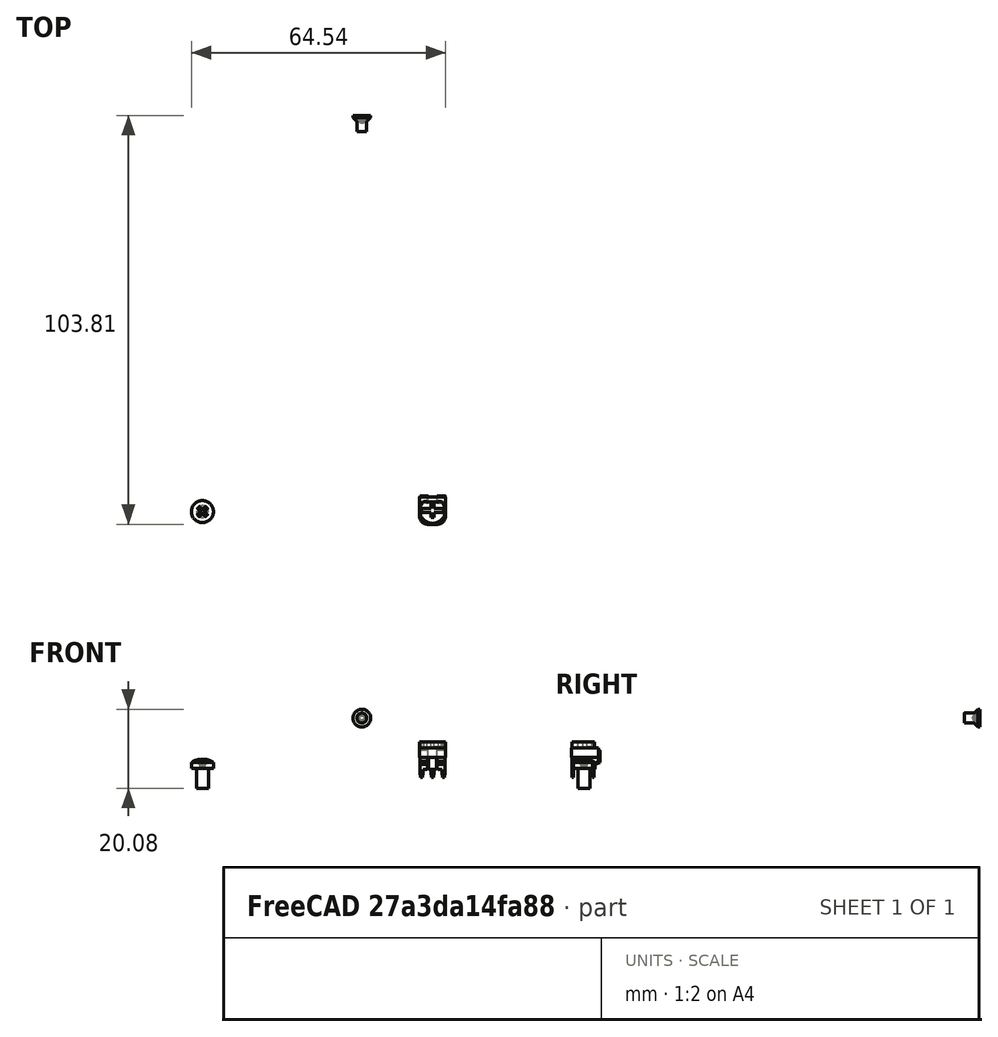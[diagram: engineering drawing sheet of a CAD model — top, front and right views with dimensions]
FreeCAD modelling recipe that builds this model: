
FCSTD DOCUMENT  (FreeCAD 0.19R23058 (Git))
Label: assembly
License: All rights reserved
LicenseURL: http://en.wikipedia.org/wiki/All_rights_reserved
objects: App::Link×8, PartDesign::CoordinateSystem×4, App::Part×4, PartDesign::Point×3, App::VRMLObject×3, App::DocumentObjectGroup×2, Part::FeaturePython×2, App::FeaturePython×1, Part::Feature×1
note: 10 computed .brp shape members not serialized (recipe doc carries the construction recipe); baked Part::Feature solids carry a one-line shape summary decoded from their .brp
EXTERNAL_REF file=parts/bottom_shell.FCStd obj=LCS_1
EXTERNAL_REF file=parts/bottom_shell.FCStd obj=Body
EXTERNAL_REF file=parts/bottom_shell.FCStd obj=HoleAxis_2
EXTERNAL_REF file=parts/top_shell.FCStd obj=HoleAxis_1
EXTERNAL_REF file=parts/top_shell.FCStd obj=Body
EXTERNAL_REF file=parts/board.FCStd obj=HoleAxis_1
EXTERNAL_REF file=parts/bottom_shell.FCStd obj=HoleAxis_16
EXTERNAL_REF file=parts/board.FCStd obj=Body
EXTERNAL_REF file=parts/top_shell.FCStd obj=Label_1
EXTERNAL_REF file=parts/top_shell.FCStd obj=Point_1
EXTERNAL_REF file=parts/bottom_shell.FCStd obj=Label_1
EXTERNAL_REF file=HB9500/assembly.FCStd obj=Contact_1
EXTERNAL_REF file=parts/board.FCStd obj=HoleAxis_2
EXTERNAL_REF file=HB9500/assembly.FCStd obj=Model
EXTERNAL_REF file=parts/top_shell.FCStd obj=HoleAxis_3
EXTERNAL_REF file=parts/top_shell.FCStd obj=HoleAxis_2
EXTERNAL_REF file=parts/bottom_shell.FCStd obj=HoleAxis_1

FEATURE [PartDesign::CoordinateSystem] LCS_Origin
  AttacherType = Attacher::AttachEngine3D
  MapMode = 2
  Support = -> [X_Axis]
FEATURE [App::DocumentObjectGroup] Constraints
FEATURE [App::FeaturePython] Variables  # WARN: FeaturePython — macro-defined, semantics opaque (R4)
FEATURE [App::Link] bottom_shell_Body
  AssemblyType = Asm4EE
  AttachedBy = #LCS_1
  AttachedTo = Parent Assembly#LCS_Origin
  LinkedObject = -> <external parts/bottom_shell.FCStd>#Body
  expr: Placement = LCS_Origin.Placement * AttachmentOffset * bottom_shell#LCS_1.Placement ^ -1
FEATURE [App::Link] top_shell_Body
  AssemblyType = Asm4EE
  AttachedBy = #HoleAxis_1
  AttachedTo = bottom_shell_Body#HoleAxis_2
  LinkPlacement = pos=(0.25,6.58371,36) rot=(0,0,1;0rad)
  LinkedObject = -> <external parts/top_shell.FCStd>#Body
  Placement = pos=(0.25,6.58371,36) rot=(0,0,1;0rad)
  expr: Placement = bottom_shell_Body.Placement * bottom_shell#HoleAxis_2.Placement * AttachmentOffset * top_shell#HoleAxis_1.Placement ^ -1
FEATURE [App::Link] board_Body
  AssemblyType = Asm4EE
  AttachedBy = #HoleAxis_1
  AttachedTo = bottom_shell_Body#HoleAxis_16
  AttachmentOffset = pos=(0,0,0) rot=(0,0,1;3.14159rad)
  LinkPlacement = pos=(0.5,-2,6) rot=(0,0,1;0rad)
  LinkedObject = -> <external parts/board.FCStd>#Body
  Placement = pos=(0.5,-2,6) rot=(0,0,1;0rad)
  expr: Placement = bottom_shell_Body.Placement * bottom_shell#HoleAxis_16.Placement * AttachmentOffset * board#HoleAxis_1.Placement ^ -1
FEATURE [Part::Feature] Part__Feature  label="Potentiometer Blue"
  Placement = pos=(25.4437,-49.9766,10.5) rot=(0,0,1;1.5708rad)
  shape: bbox 6.6 x 7.2 x 9 mm, 74 faces, 2 solids (baked)
FEATURE [PartDesign::Point] Point_1
  AttacherType = Attacher::AttachEnginePoint
  Placement = pos=(-32,-36.6163,25.5) rot=(0,0,1;0rad)
  expr: Placement = top_shell_Body.Placement * top_shell#Label_1.Placement * AttachmentOffset
FEATURE [PartDesign::CoordinateSystem] LCS_0
  AttacherType = Attacher::AttachEngine3D
  AttachmentOffset = pos=(65,10,0) rot=(0,0,1;3.14159rad)
  MapMode = 2
  Placement = pos=(65,10,0) rot=(0,0,1;3.14159rad)
  Support = -> [X_Axis001]
FEATURE [App::VRMLObject] label_1
  Resources = label_1/label_1.jpg
FEATURE [App::Part] Part  label="Label_1"
  Group = -> [LCS_0,label_1]
  Origin = -> Origin001
FEATURE [App::Link] Link  label="Label_002"
  AssemblyType = Asm4EE
  AttachedBy = #LCS_0
  AttachedTo = top_shell_Body#Label_1
  AttachmentOffset = pos=(0,0,0) rot=(1,0,0;1.5708rad)
  LinkPlacement = pos=(33,-36.6163,35.5) rot=(0,0.707107,-0.707107;3.14159rad)
  LinkedObject = -> Part
  Placement = pos=(33,-36.6163,35.5) rot=(0,0.707107,-0.707107;3.14159rad)
  expr: Placement = top_shell_Body.Placement * top_shell#Label_1.Placement * AttachmentOffset * LCS_0.Placement ^ -1
FEATURE [PartDesign::CoordinateSystem] LCS_0001
  AttacherType = Attacher::AttachEngine3D
  AttachmentOffset = pos=(32,14,0) rot=(0,0,1;3.14159rad)
  MapMode = 2
  Placement = pos=(32,14,0) rot=(0,0,1;3.14159rad)
  Support = -> [X_Axis002]
FEATURE [App::VRMLObject] label_2
  Resources = label_2/label_2.jpg
FEATURE [App::Part] Part_2  label="Label_2"
  Group = -> [LCS_0001,label_2]
  Origin = -> Origin002
  Placement = pos=(73,0,0) rot=(0,0,1;0rad)
FEATURE [App::Link] Link001  label="Label_003"
  AssemblyType = Asm4EE
  AttachedBy = #LCS_0001
  AttachedTo = top_shell_Body#Point_1
  LinkPlacement = pos=(-2.5,-20.9163,36) rot=(0,0,-1;3.14159rad)
  LinkedObject = -> Part_2
  Placement = pos=(-2.5,-20.9163,36) rot=(0,0,-1;3.14159rad)
  expr: Placement = top_shell_Body.Placement * top_shell#Point_1.Placement * AttachmentOffset * LCS_0001.Placement ^ -1
FEATURE [PartDesign::Point] Point_2
  AttacherType = Attacher::AttachEnginePoint
  Placement = pos=(-34.5,-34.9163,36) rot=(0,0,1;0rad)
  expr: Placement = top_shell_Body.Placement * top_shell#Point_1.Placement * AttachmentOffset
FEATURE [PartDesign::CoordinateSystem] LCS_0002
  AttacherType = Attacher::AttachEngine3D
  MapMode = 2
  Support = -> [X_Axis003]
FEATURE [App::VRMLObject] label_3
  Resources = label_3/label_3.jpg
FEATURE [App::Part] Label_3
  Group = -> [LCS_0002,label_3]
  Origin = -> Origin003
  Placement = pos=(79,0,0) rot=(0,0,1;0rad)
FEATURE [App::DocumentObjectGroup] Parts
  Group = -> [Part,Part_2,Label_3]
FEATURE [PartDesign::Point] Label_3001
  AttacherType = Attacher::AttachEnginePoint
  Placement = pos=(39.5,20,33) rot=(0,0,1;0rad)
  expr: Placement = bottom_shell_Body.Placement * bottom_shell#Label_1.Placement * AttachmentOffset
FEATURE [App::Link] Link002  label="Label_3002"
  AssemblyType = Asm4EE
  AttachedBy = #LCS_0002
  AttachedTo = bottom_shell_Body#Label_1
  AttachmentOffset = pos=(0,0,0) rot=(0.57735,-0.57735,0.57735;4.18879rad)
  LinkPlacement = pos=(39.5,20,33) rot=(0.57735,-0.57735,0.57735;4.18879rad)
  LinkedObject = -> Label_3
  Placement = pos=(39.5,20,33) rot=(0.57735,-0.57735,0.57735;4.18879rad)
  expr: Placement = bottom_shell_Body.Placement * bottom_shell#Label_1.Placement * AttachmentOffset * LCS_0002.Placement ^ -1
FEATURE [App::Link] assembly1
  AssemblyType = Asm4EE
  AttachedBy = #Contact_1
  AttachedTo = board_Body#HoleAxis_2
  LinkPlacement = pos=(-4,-46.5,7.5) rot=(0,0,1;0rad)
  LinkedObject = -> <external HB9500/assembly.FCStd>#Model
  Placement = pos=(-4,-46.5,7.5) rot=(0,0,1;0rad)
  expr: Placement = board_Body.Placement * board#HoleAxis_2.Placement * AttachmentOffset * assembly1#Contact_1.Placement ^ -1
FEATURE [Part::FeaturePython] Screw  label="M3x5-Screw"  # Fasteners workbench fastener (typed FeaturePython)
  AssemblyType = Asm4EE
  AttachedBy = Origin
  AttachedTo = top_shell_Body#HoleAxis_2
  Placement = pos=(-33,-50.2163,7.7) rot=(0,0,1;3.14159rad)
  diameter = 4
  invert = false
  length = 1
  lengthCustom = 5
  matchOuter = false
  offset = 0
  thread = false
  type = 33
  expr: Placement = top_shell_Body.Placement * top_shell#HoleAxis_3.Placement * AttachmentOffset
FEATURE [App::Link] Screw001  label="M3x5-Screw001"
  LinkPlacement = pos=(-32.5,49.5837,21) rot=(-1,0,0;1.5708rad)
  LinkedObject = -> Screw
  Placement = pos=(-32.5,49.5837,21) rot=(-1,0,0;1.5708rad)
  expr: Placement = top_shell_Body.Placement * top_shell#HoleAxis_2.Placement * AttachmentOffset
FEATURE [Part::FeaturePython] Screw002  label="M2.5x4-Screw"  # Fasteners workbench fastener (typed FeaturePython)
  AssemblyType = Asm4EE
  AttachedBy = Origin
  AttachedTo = bottom_shell_Body#HoleAxis_1
  AttachmentOffset = pos=(0,0,1) rot=(0,0,1;0rad)
  Placement = pos=(7.5,50.3837,20.5321) rot=(-1,0,0;1.5708rad)
  diameter = 3
  invert = false
  length = 1
  lengthCustom = 4
  matchOuter = false
  offset = 0
  thread = false
  type = 34
  expr: Placement = bottom_shell_Body.Placement * bottom_shell#HoleAxis_1.Placement * AttachmentOffset
FEATURE [App::Part] Model
  Configuration = 0
  Group = -> [LCS_Origin,Constraints,Variables,bottom_shell_Body,top_shell_Body,board_Body,Part__Feature,Point_1,Link,Link001,Point_2,Label_3001,Link002,assembly1,Screw,Screw001,Screw002]
  Origin = -> Origin
  Type = Assembly4 Model

RESOLVED EXTERNAL PARTS (link-assembly join: the EXTERNAL_REF files above that resolve inside this repo's crawl, each included once):
---- part HB9500/assembly.FCStd = doc fcstd_5ce3ce619bd0 ----
FCSTD DOCUMENT  (FreeCAD 0.19R23058 (Git))
Label: assembly
License: All rights reserved
LicenseURL: http://en.wikipedia.org/wiki/All_rights_reserved
objects: App::Link×17, App::DocumentObjectGroup×2, PartDesign::CoordinateSystem×1, App::FeaturePython×1, PartDesign::Line×1, App::Part×1
note: 2 computed .brp shape members not serialized (recipe doc carries the construction recipe); baked Part::Feature solids carry a one-line shape summary decoded from their .brp
EXTERNAL_REF file=parts/main.FCStd obj=LCS_1
EXTERNAL_REF file=parts/main.FCStd obj=Body
EXTERNAL_REF file=parts/cover.FCStd obj=HoleAxis_1
EXTERNAL_REF file=parts/main.FCStd obj=HoleAxis_6
EXTERNAL_REF file=parts/cover.FCStd obj=Body
EXTERNAL_REF file=parts/bottom_contact.FCStd obj=HoleAxis_2
EXTERNAL_REF file=parts/main.FCStd obj=HoleAxis_1
EXTERNAL_REF file=parts/bottom_contact.FCStd obj=Body
EXTERNAL_REF file=parts/main.FCStd obj=HoleAxis_2
EXTERNAL_REF file=parts/main.FCStd obj=HoleAxis_3
EXTERNAL_REF file=parts/main.FCStd obj=HoleAxis_4
EXTERNAL_REF file=parts/main.FCStd obj=HoleAxis_5
EXTERNAL_REF file=parts/bottom_contact.FCStd obj=HoleAxis_1
EXTERNAL_REF file=parts/top_contact.FCStd obj=Screw_R
EXTERNAL_REF file=parts/top_contact.FCStd obj=Body
EXTERNAL_REF file=parts/screw.FCStd obj=HoleAxis_1
EXTERNAL_REF file=parts/top_contact.FCStd obj=Screw_F
EXTERNAL_REF file=parts/screw.FCStd obj=Body
EXTERNAL_REF file=parts/bottom_contact.FCStd obj=Contact

FEATURE [App::DocumentObjectGroup] Parts
FEATURE [PartDesign::CoordinateSystem] LCS_Origin
  AttacherType = Attacher::AttachEngine3D
  MapMode = 2
  Support = -> [X_Axis]
FEATURE [App::DocumentObjectGroup] Constraints
FEATURE [App::FeaturePython] Variables  # WARN: FeaturePython — macro-defined, semantics opaque (R4)
FEATURE [App::Link] main_Body
  AssemblyType = Asm4EE
  AttachedBy = #LCS_1
  AttachedTo = Parent Assembly#LCS_Origin
  LinkedObject = -> <external parts/main.FCStd>#Body
  expr: Placement = LCS_Origin.Placement * AttachmentOffset * main#LCS_1.Placement ^ -1
FEATURE [App::Link] cover_Body
  AssemblyType = Asm4EE
  AttachedBy = #HoleAxis_1
  AttachedTo = main_Body#HoleAxis_6
  AttachmentOffset = pos=(0,0,0.7) rot=(0,0,1;0rad)
  LinkPlacement = pos=(1.07e-14,1.24e-14,15.5) rot=(0,0,1;0rad)
  LinkedObject = -> <external parts/cover.FCStd>#Body
  Placement = pos=(1.07e-14,1.24e-14,15.5) rot=(0,0,1;0rad)
  expr: Placement = main_Body.Placement * main#HoleAxis_6.Placement * AttachmentOffset * cover#HoleAxis_1.Placement ^ -1
FEATURE [App::Link] bottom_contact_Body
  AssemblyType = Asm4EE
  AttachedBy = #HoleAxis_2
  AttachedTo = main_Body#HoleAxis_1
  LinkPlacement = pos=(-19,-1.05,9.3) rot=(0,0,1;0rad)
  LinkedObject = -> <external parts/bottom_contact.FCStd>#Body
  Placement = pos=(-19,-1.05,9.3) rot=(0,0,1;0rad)
  expr: Placement = main_Body.Placement * main#HoleAxis_1.Placement * AttachmentOffset * bottom_contact#HoleAxis_2.Placement ^ -1
FEATURE [App::Link] bottom_contact_Body001
  AssemblyType = Asm4EE
  AttachedBy = #HoleAxis_2
  AttachedTo = main_Body#HoleAxis_2
  LinkPlacement = pos=(-9.5,-1.05,9.3) rot=(0,0,1;0rad)
  LinkedObject = -> <external parts/bottom_contact.FCStd>#Body
  Placement = pos=(-9.5,-1.05,9.3) rot=(0,0,1;0rad)
  expr: Placement = main_Body.Placement * main#HoleAxis_2.Placement * AttachmentOffset * bottom_contact#HoleAxis_2.Placement ^ -1
FEATURE [App::Link] bottom_contact_Body002
  AssemblyType = Asm4EE
  AttachedBy = #HoleAxis_2
  AttachedTo = main_Body#HoleAxis_3
  LinkPlacement = pos=(-8e-16,-1.05,9.3) rot=(0,0,1;0rad)
  LinkedObject = -> <external parts/bottom_contact.FCStd>#Body
  Placement = pos=(-8e-16,-1.05,9.3) rot=(0,0,1;0rad)
  expr: Placement = main_Body.Placement * main#HoleAxis_3.Placement * AttachmentOffset * bottom_contact#HoleAxis_2.Placement ^ -1
FEATURE [App::Link] bottom_contact_Body003
  AssemblyType = Asm4EE
  AttachedBy = #HoleAxis_2
  AttachedTo = main_Body#HoleAxis_4
  LinkPlacement = pos=(9.5,-1.05,9.3) rot=(0,0,1;0rad)
  LinkedObject = -> <external parts/bottom_contact.FCStd>#Body
  Placement = pos=(9.5,-1.05,9.3) rot=(0,0,1;0rad)
  expr: Placement = main_Body.Placement * main#HoleAxis_4.Placement * AttachmentOffset * bottom_contact#HoleAxis_2.Placement ^ -1
FEATURE [App::Link] bottom_contact_Body004
  AssemblyType = Asm4EE
  AttachedBy = #HoleAxis_2
  AttachedTo = main_Body#HoleAxis_5
  LinkPlacement = pos=(19,-1.05,9.3) rot=(0,0,1;0rad)
  LinkedObject = -> <external parts/bottom_contact.FCStd>#Body
  Placement = pos=(19,-1.05,9.3) rot=(0,0,1;0rad)
  expr: Placement = main_Body.Placement * main#HoleAxis_5.Placement * AttachmentOffset * bottom_contact#HoleAxis_2.Placement ^ -1
FEATURE [App::Link] top_contact_Body
  AssemblyType = Asm4EE
  AttachedBy = #Screw_R
  AttachedTo = bottom_contact_Body#HoleAxis_1
  LinkPlacement = pos=(-19,-1.05,9.42306) rot=(0,0,-1;1.5708rad)
  LinkedObject = -> <external parts/top_contact.FCStd>#Body
  Placement = pos=(-19,-1.05,9.42306) rot=(0,0,-1;1.5708rad)
  expr: Placement = bottom_contact_Body.Placement * bottom_contact#HoleAxis_1.Placement * AttachmentOffset * top_contact#Screw_R.Placement ^ -1
FEATURE [App::Link] top_contact_Body001
  AssemblyType = Asm4EE
  AttachedBy = #Screw_R
  AttachedTo = bottom_contact_Body001#HoleAxis_1
  LinkPlacement = pos=(-9.5,-1.05,9.42306) rot=(0,0,-1;1.5708rad)
  LinkedObject = -> <external parts/top_contact.FCStd>#Body
  Placement = pos=(-9.5,-1.05,9.42306) rot=(0,0,-1;1.5708rad)
  expr: Placement = bottom_contact_Body001.Placement * bottom_contact#HoleAxis_1.Placement * AttachmentOffset * top_contact#Screw_R.Placement ^ -1
FEATURE [App::Link] top_contact_Body002
  AssemblyType = Asm4EE
  AttachedBy = #Screw_R
  AttachedTo = bottom_contact_Body002#HoleAxis_1
  LinkPlacement = pos=(1.01405e-07,-1.05,9.42306) rot=(0,0,-1;1.5708rad)
  LinkedObject = -> <external parts/top_contact.FCStd>#Body
  Placement = pos=(1.01405e-07,-1.05,9.42306) rot=(0,0,-1;1.5708rad)
  expr: Placement = bottom_contact_Body002.Placement * bottom_contact#HoleAxis_1.Placement * AttachmentOffset * top_contact#Screw_R.Placement ^ -1
FEATURE [App::Link] top_contact_Body003
  AssemblyType = Asm4EE
  AttachedBy = #Screw_R
  AttachedTo = bottom_contact_Body003#HoleAxis_1
  LinkPlacement = pos=(9.5,-1.05,9.42306) rot=(0,0,-1;1.5708rad)
  LinkedObject = -> <external parts/top_contact.FCStd>#Body
  Placement = pos=(9.5,-1.05,9.42306) rot=(0,0,-1;1.5708rad)
  expr: Placement = bottom_contact_Body003.Placement * bottom_contact#HoleAxis_1.Placement * AttachmentOffset * top_contact#Screw_R.Placement ^ -1
FEATURE [App::Link] top_contact_Body004
  AssemblyType = Asm4EE
  AttachedBy = #Screw_R
  AttachedTo = bottom_contact_Body004#HoleAxis_1
  LinkPlacement = pos=(19,-1.05,9.42306) rot=(0,0,-1;1.5708rad)
  LinkedObject = -> <external parts/top_contact.FCStd>#Body
  Placement = pos=(19,-1.05,9.42306) rot=(0,0,-1;1.5708rad)
  expr: Placement = bottom_contact_Body004.Placement * bottom_contact#HoleAxis_1.Placement * AttachmentOffset * top_contact#Screw_R.Placement ^ -1
FEATURE [App::Link] screw_Body
  AssemblyType = Asm4EE
  AttachedBy = #HoleAxis_1
  AttachedTo = top_contact_Body#Screw_F
  LinkPlacement = pos=(-19,-1.05001,11.2846) rot=(0,0,-1;1.5708rad)
  LinkedObject = -> <external parts/screw.FCStd>#Body
  Placement = pos=(-19,-1.05001,11.2846) rot=(0,0,-1;1.5708rad)
  expr: Placement = top_contact_Body.Placement * top_contact#Screw_F.Placement * AttachmentOffset * screw#HoleAxis_1.Placement ^ -1
FEATURE [App::Link] screw_Body001
  AssemblyType = Asm4EE
  AttachedBy = #HoleAxis_1
  AttachedTo = top_contact_Body001#Screw_F
  LinkPlacement = pos=(-9.5,-1.05001,11.2846) rot=(0,0,-1;1.5708rad)
  LinkedObject = -> <external parts/screw.FCStd>#Body
  Placement = pos=(-9.5,-1.05001,11.2846) rot=(0,0,-1;1.5708rad)
  expr: Placement = top_contact_Body001.Placement * top_contact#Screw_F.Placement * AttachmentOffset * screw#HoleAxis_1.Placement ^ -1
FEATURE [App::Link] screw_Body002
  AssemblyType = Asm4EE
  AttachedBy = #HoleAxis_1
  AttachedTo = top_contact_Body002#Screw_F
  LinkPlacement = pos=(-5.53414e-09,-1.05001,11.2846) rot=(0,0,-1;1.5708rad)
  LinkedObject = -> <external parts/screw.FCStd>#Body
  Placement = pos=(-5.53414e-09,-1.05001,11.2846) rot=(0,0,-1;1.5708rad)
  expr: Placement = top_contact_Body002.Placement * top_contact#Screw_F.Placement * AttachmentOffset * screw#HoleAxis_1.Placement ^ -1
FEATURE [App::Link] screw_Body003
  AssemblyType = Asm4EE
  AttachedBy = #HoleAxis_1
  AttachedTo = top_contact_Body003#Screw_F
  LinkPlacement = pos=(9.5,-1.05001,11.2846) rot=(0,0,-1;1.5708rad)
  LinkedObject = -> <external parts/screw.FCStd>#Body
  Placement = pos=(9.5,-1.05001,11.2846) rot=(0,0,-1;1.5708rad)
  expr: Placement = top_contact_Body003.Placement * top_contact#Screw_F.Placement * AttachmentOffset * screw#HoleAxis_1.Placement ^ -1
FEATURE [App::Link] screw_Body004
  AssemblyType = Asm4EE
  AttachedBy = #HoleAxis_1
  AttachedTo = top_contact_Body004#Screw_F
  LinkPlacement = pos=(19,-1.05001,11.2846) rot=(0,0,-1;1.5708rad)
  LinkedObject = -> <external parts/screw.FCStd>#Body
  Placement = pos=(19,-1.05001,11.2846) rot=(0,0,-1;1.5708rad)
  expr: Placement = top_contact_Body004.Placement * top_contact#Screw_F.Placement * AttachmentOffset * screw#HoleAxis_1.Placement ^ -1
FEATURE [PartDesign::Line] Contact_1
  AttacherType = Attacher::AttachEngineLine
  Length = 5
  Placement = pos=(-19,4,-2.0997e-12) rot=(0,0,1;0rad)
  ResizeMode = 1
  expr: Placement = bottom_contact_Body.Placement * bottom_contact#Contact.Placement * AttachmentOffset
FEATURE [App::Part] Model
  Configuration = 0
  Group = -> [LCS_Origin,Constraints,Variables,main_Body,cover_Body,bottom_contact_Body,bottom_contact_Body001,bottom_contact_Body002,bottom_contact_Body003,bottom_contact_Body004,top_contact_Body,top_contact_Body001,top_contact_Body002,top_contact_Body003,top_contact_Body004,screw_Body,screw_Body001,screw_Body002,screw_Body003,screw_Body004,Contact_1]
  Origin = -> Origin
  Type = Assembly4 Model
---- part parts/board.FCStd = doc fcstd_48fc7f9aef9a ----
FCSTD DOCUMENT  (FreeCAD 0.19R23058 (Git))
Label: board
License: All rights reserved
LicenseURL: http://en.wikipedia.org/wiki/All_rights_reserved
objects: PartDesign::Line×2, Sketcher::SketchObject×1, PartDesign::Pad×1, PartDesign::Body×1
note: 6 computed .brp shape members not serialized (recipe doc carries the construction recipe); baked Part::Feature solids carry a one-line shape summary decoded from their .brp

FEATURE [Sketcher::SketchObject] Sketch
  MapMode = 5
  Support = -> [XY_Plane]
  sketch-geometry (17):
    g0: LineSegment StartX=-37.5 StartY=52.5 StartZ=0 EndX=37.5 EndY=52.5 EndZ=0
    g1: LineSegment StartX=37.5 StartY=52.5 StartZ=0 EndX=37.5 EndY=-42.5 EndZ=0
    g2: LineSegment StartX=29.5 StartY=-52.5 StartZ=0 EndX=-37.5 EndY=-52.5 EndZ=0
    g3: LineSegment StartX=-37.5 StartY=-52.5 StartZ=0 EndX=-37.5 EndY=52.5 EndZ=0
    g4: Circle CenterX=-33.5 CenterY=-48 CenterZ=0 NormalX=0 NormalY=0 NormalZ=1 AngleXU=0 Radius=1.75
    g5: Circle CenterX=-30.8 CenterY=45 CenterZ=0 NormalX=0 NormalY=0 NormalZ=1 AngleXU=0 Radius=1.75
    g6: LineSegment StartX=29.5 StartY=-52.5 StartZ=0 EndX=29.5 EndY=-42.5 EndZ=0
    g7: LineSegment StartX=29.5 StartY=-42.5 StartZ=0 EndX=37.5 EndY=-42.5 EndZ=0
    g8: LineSegment [constr] StartX=-23.5 StartY=-40.5 StartZ=0 EndX=-14 EndY=-40.5 EndZ=0
    g9: LineSegment [constr] StartX=-14 StartY=-40.5 StartZ=0 EndX=-4.5 EndY=-40.5 EndZ=0
    g10: LineSegment [constr] StartX=-4.5 StartY=-40.5 StartZ=0 EndX=5 EndY=-40.5 EndZ=0
    g11: LineSegment [constr] StartX=5 StartY=-40.5 StartZ=0 EndX=14.5 EndY=-40.5 EndZ=0
    g12: Circle CenterX=-23.5 CenterY=-40.5 CenterZ=0 NormalX=0 NormalY=0 NormalZ=1 AngleXU=0 Radius=0.5
    g13: Circle CenterX=-14 CenterY=-40.5 CenterZ=0 NormalX=0 NormalY=0 NormalZ=1 AngleXU=0 Radius=0.5
    g14: Circle CenterX=-4.5 CenterY=-40.5 CenterZ=0 NormalX=0 NormalY=0 NormalZ=1 AngleXU=0 Radius=0.5
    g15: Circle CenterX=5 CenterY=-40.5 CenterZ=0 NormalX=0 NormalY=0 NormalZ=1 AngleXU=0 Radius=0.5
    g16: Circle CenterX=14.5 CenterY=-40.5 CenterZ=0 NormalX=0 NormalY=0 NormalZ=1 AngleXU=0 Radius=0.5
  constraints (45):
    c: Coincident(g0,g1)
    c: Coincident(g2,g3)
    c: Coincident(g3,g0)
    c: Horizontal(g2)
    c: Vertical(g1)
    c: Symmetric(g0,g2,g-1)
    c: Symmetric(g0,g0,g-2)
    c: DistanceY(g3,g3) = 105
    c: Coincident(g2,g6)
    c: Coincident(g6,g7)
    c: Coincident(g7,g1)
    c: Horizontal(g7)
    c: Vertical(g6)
    c: DistanceX(g0,g0) = 75
    c: DistanceY(g6,g6) = 10
    c: DistanceX(g7,g7) = 8
    c: Radius(g4) = 1.75
    c: Equal(g4,g5)
    c: DistanceY(g2,g4) = 4.5
    c: DistanceX(g2,g4) = 4
    c: DistanceY(g5,g0) = 7.5
    c: DistanceX(g0,g5) = 6.7
    c: Horizontal(g8)
    c: Coincident(g8,g9)
    c: Horizontal(g9)
    c: Coincident(g9,g10)
    c: Horizontal(g10)
    c: Coincident(g10,g11)
    c: Horizontal(g11)
    c: DistanceX(g8,g8) = 9.5
    c: Equal(g8,g9)
    c: Equal(g9,g10)
    c: Equal(g10,g11)
    c: DistanceY(g2,g8) = 12
    c: DistanceX(g2,g8) = 14
    c: Coincident(g12,g8)
    c: Coincident(g13,g8)
    c: Coincident(g14,g9)
    c: Coincident(g15,g10)
    c: Coincident(g16,g11)
    c: Radius(g16) = 0.5
    c: Equal(g16,g15)
    c: Equal(g15,g14)
    c: Equal(g14,g13)
    c: Equal(g13,g12)
FEATURE [PartDesign::Pad] Pad
  Direction = (1,1,1)
  Length = 1.5
  Length2 = 100
  Profile = -> Sketch
  Type = 0
FEATURE [PartDesign::Line] HoleAxis_1  label="Fastnr_1"
  AttacherType = Attacher::AttachEngineLine
  Length = 4.93174
  MapMode = 19
  Placement = pos=(-33.5,-48,0) rot=(0,0,1;0rad)
  ResizeMode = 1
  Support = -> [Pad]
FEATURE [PartDesign::Line] HoleAxis_2  label="Contact_1"
  AttacherType = Attacher::AttachEngineLine
  Length = 1.40907
  MapMode = 19
  Placement = pos=(-23.5,-40.5,1.5) rot=(0,0,1;0rad)
  ResizeMode = 1
  Support = -> [Pad]
FEATURE [PartDesign::Body] Body
  Group = -> [Sketch,Pad,HoleAxis_1,HoleAxis_2]
  Origin = -> Origin
  Tip = -> Pad
---- part parts/bottom_shell.FCStd = doc fcstd_8761fee64455 ----
FCSTD DOCUMENT  (FreeCAD 0.19R23058 (Git))
Label: bottom_shell
License: All rights reserved
LicenseURL: http://en.wikipedia.org/wiki/All_rights_reserved
objects: PartDesign::Line×17, Sketcher::SketchObject×9, PartDesign::Pocket×5, PartDesign::Pad×4, PartDesign::Plane×1, PartDesign::CoordinateSystem×1, PartDesign::Point×1, PartDesign::Body×1
note: 48 computed .brp shape members not serialized (recipe doc carries the construction recipe); baked Part::Feature solids carry a one-line shape summary decoded from their .brp

FEATURE [Sketcher::SketchObject] Sketch
  MapMode = 5
  Placement = pos=(0,0,0) rot=(1,0,0;1.5708rad)
  Support = -> [XZ_Plane]
  sketch-geometry (8):
    g0: LineSegment StartX=-38 StartY=1 StartZ=0 EndX=-38 EndY=0 EndZ=0
    g1: LineSegment StartX=-38 StartY=0 StartZ=0 EndX=38 EndY=0 EndZ=0
    g2: LineSegment StartX=39.5 StartY=1.5 StartZ=0 EndX=39.5 EndY=36 EndZ=0
    g3: LineSegment StartX=39.5 StartY=36 StartZ=0 EndX=38.5 EndY=36 EndZ=0
    g4: LineSegment StartX=38.5 StartY=36 StartZ=0 EndX=38.5 EndY=1.5 EndZ=0
    g5: LineSegment StartX=38 StartY=1 StartZ=0 EndX=-38 EndY=1 EndZ=0
    g6: ArcOfCircle CenterX=38 CenterY=1.5 CenterZ=0 NormalX=0 NormalY=0 NormalZ=1 AngleXU=0 Radius=0.5 StartAngle=4.71239 EndAngle=6.28319
    g7: ArcOfCircle CenterX=38 CenterY=1.5 CenterZ=0 NormalX=0 NormalY=0 NormalZ=1 AngleXU=0 Radius=1.5 StartAngle=4.71239 EndAngle=6.28319
  constraints (20):
    c: Coincident(g0,g1)
    c: Vertical(g2)
    c: Coincident(g2,g3)
    c: Coincident(g3,g4)
    c: Vertical(g4)
    c: Coincident(g5,g0)
    c: Horizontal(g5)
    c: Tangent(g5,g6) = 1.5708
    c: Tangent(g4,g6) = 1.5708
    c: Tangent(g1,g7) = -1.5708
    c: Tangent(g2,g7) = -1.5708
    c: Vertical(g0)
    c: Horizontal(g3)
    c: PointOnObject(g0,g-1)
    c: Symmetric(g0,g1,g-2)
    c: DistanceY(g0,g0) = 1
    c: Radius(g7) = 1.5
    c: DistanceX(g1,g1) = 76
    c: DistanceY(g2,g2) = 34.5
    c: Coincident(g6,g7)
FEATURE [PartDesign::Pad] Pad
  Direction = (1,1,1)
  Length = 110
  Length2 = 100
  Midplane = true
  Placement = pos=(0,0,0) rot=(1,0,0;1.5708rad)
  Profile = -> Sketch
  Type = 0
FEATURE [Sketcher::SketchObject] Sketch001
  ExternalGeometry = -> [Pad]
  MapMode = 5
  Placement = pos=(39.5,0,0) rot=(0.707107,0,0.707107;3.14159rad)
  Support = -> [Pad]
  sketch-geometry (4):
    g0: LineSegment StartX=-4.55e-14 StartY=-53 StartZ=0 EndX=2 EndY=-53 EndZ=0
    g1: LineSegment StartX=2 StartY=-53 StartZ=0 EndX=2 EndY=-55 EndZ=0
    g2: LineSegment StartX=2 StartY=-55 StartZ=0 EndX=-4.55e-14 EndY=-55 EndZ=0
    g3: LineSegment StartX=-4.55e-14 StartY=-55 StartZ=0 EndX=-4.55e-14 EndY=-53 EndZ=0
  constraints (11):
    c: Coincident(g0,g1)
    c: Coincident(g1,g2)
    c: Coincident(g2,g3)
    c: Coincident(g3,g0)
    c: Horizontal(g0)
    c: Horizontal(g2)
    c: Vertical(g1)
    c: Vertical(g3)
    c: DistanceX(g2,g2) = 2
    c: Equal(g2,g1)
    c: Coincident(g2,g-3)
FEATURE [PartDesign::Pocket] Pocket
  BaseFeature = -> Pad
  Length = 68.5
  Length2 = 100
  Placement = pos=(0,0,0) rot=(1,0,0;1.5708rad)
  Profile = -> Sketch001
  Type = 0
FEATURE [PartDesign::Plane] DatumPlane
  AttachmentOffset = pos=(0,0,-2) rot=(0,0,1;0rad)
  Length = 60
  MapMode = 5
  Placement = pos=(37.5,0,4e-16) rot=(0.707107,0,0.707107;3.14159rad)
  ResizeMode = 0
  Support = -> [Pocket]
  Width = 60
FEATURE [Sketcher::SketchObject] Sketch002
  ExternalGeometry = -> [Pocket]
  MapMode = 5
  Placement = pos=(37.5,0,4e-16) rot=(0.707107,0,0.707107;3.14159rad)
  Support = -> [DatumPlane]
  sketch-geometry (14):
    g0: ArcOfCircle CenterX=2 CenterY=-53 CenterZ=0 NormalX=0 NormalY=0 NormalZ=1 AngleXU=0 Radius=2 StartAngle=3.1416 EndAngle=4.71239
    g1: LineSegment StartX=2 StartY=-55 StartZ=0 EndX=6.48793 EndY=-55 EndZ=0
    g2: ArcOfCircle CenterX=6.48793 CenterY=-52 CenterZ=0 NormalX=0 NormalY=0 NormalZ=1 AngleXU=0 Radius=3 StartAngle=4.71239 EndAngle=5.58505
    g3: LineSegment StartX=8.78606 StartY=-53.9284 StartZ=0 EndX=12 EndY=-50.0981 EndZ=0
    g4: ArcOfCircle CenterX=13.5321 CenterY=-51.3837 CenterZ=0 NormalX=0 NormalY=0 NormalZ=1 AngleXU=0 Radius=2 StartAngle=1.5708 EndAngle=2.44346
    g5: LineSegment StartX=13.5321 StartY=-49.3837 StartZ=0 EndX=32.5321 EndY=-49.3837 EndZ=0
    g6: LineSegment StartX=32.5321 StartY=-49.3837 StartZ=0 EndX=32.5321 EndY=-48.3837 EndZ=0
    g7: LineSegment StartX=32.5321 StartY=-48.3837 StartZ=0 EndX=13.5321 EndY=-48.3837 EndZ=0
    g8: LineSegment StartX=11.234 StartY=-49.4553 StartZ=0 EndX=8.02002 EndY=-53.2856 EndZ=0
    g9: LineSegment StartX=6.48793 StartY=-54 StartZ=0 EndX=2 EndY=-54 EndZ=0
    g10: ArcOfCircle CenterX=13.5321 CenterY=-51.3837 CenterZ=0 NormalX=0 NormalY=0 NormalZ=1 AngleXU=0 Radius=3 StartAngle=1.5708 EndAngle=2.44346
    g11: ArcOfCircle CenterX=6.48793 CenterY=-52 CenterZ=0 NormalX=0 NormalY=0 NormalZ=1 AngleXU=0 Radius=2 StartAngle=4.71239 EndAngle=5.58505
    g12: ArcOfCircle CenterX=2 CenterY=-53 CenterZ=0 NormalX=0 NormalY=0 NormalZ=1 AngleXU=0 Radius=1 StartAngle=3.1416 EndAngle=4.71239
    g13: LineSegment StartX=1.47167e-11 StartY=-53 StartZ=0 EndX=1 EndY=-53 EndZ=0
  constraints (34):
    c: Horizontal(g1)
    c: Horizontal(g5)
    c: Coincident(g5,g6)
    c: Vertical(g6)
    c: Coincident(g6,g7)
    c: Horizontal(g7)
    c: Horizontal(g9)
    c: Tangent(g0,g1) = -1.5708
    c: Tangent(g1,g2) = -1.5708
    c: Tangent(g2,g3) = -1.5708
    c: Tangent(g3,g4) = 1.5708
    c: Tangent(g4,g5) = 1.5708
    c: Coincident(g13,g0)
    c: Coincident(g13,g12)
    c: Horizontal(g13)
    c: Tangent(g12,g9) = 1.5708
    c: Tangent(g9,g11) = 1.5708
    c: Tangent(g11,g8) = 1.5708
    c: Tangent(g8,g10) = -1.5708
    c: Tangent(g10,g7) = -1.5708
    c: Tangent(g0,g-2)
    c: DistanceX(g13,g13) = 1
    c: Coincident(g0,g12)
    c: Coincident(g2,g11)
    c: Coincident(g4,g10)
    c: Parallel(g8,g3)
    c: Radius(g0) = 2
    c: Distance(g3) = 5
    c: DistanceX(g5,g5) = 19
    c: Angle(g3,g-2) = 0.698132
    c: Equal(g2,g10)
    c: Radius(g2) = 3
    c: Coincident(g0,g-3)
    c: DistanceX(g0,g3) = 12
FEATURE [PartDesign::Pad] Pad001
  BaseFeature = -> Pocket
  Direction = (1,1,1)
  Length = 65
  Length2 = 100
  Placement = pos=(0,0,0) rot=(1,0,0;1.5708rad)
  Profile = -> Sketch002
  Reversed = true
  Type = 0
FEATURE [Sketcher::SketchObject] Sketch003
  ExternalGeometry = -> [Pad001]
  MapMode = 5
  Placement = pos=(-27.5,1.35e-14,9.4e-15) rot=(-0.707107,0,0.707107;3.14159rad)
  Support = -> [Pad001]
  sketch-geometry (4):
    g0: LineSegment StartX=-32.5321 StartY=-48.3837 StartZ=0 EndX=-13.0321 EndY=-48.3837 EndZ=0
    g1: LineSegment StartX=-13.0321 StartY=-48.3837 StartZ=0 EndX=-13.0321 EndY=-49.3837 EndZ=0
    g2: LineSegment StartX=-13.0321 StartY=-49.3837 StartZ=0 EndX=-32.5321 EndY=-49.3837 EndZ=0
    g3: LineSegment StartX=-32.5321 StartY=-49.3837 StartZ=0 EndX=-32.5321 EndY=-48.3837 EndZ=0
  constraints (10):
    c: Coincident(g0,g1)
    c: Coincident(g1,g2)
    c: Coincident(g2,g3)
    c: Coincident(g3,g0)
    c: Horizontal(g0)
    c: Horizontal(g2)
    c: Vertical(g1)
    c: Coincident(g0,g-3)
    c: Coincident(g2,g-3)
    c: DistanceX(g2,g2) = 19.5
FEATURE [PartDesign::Pad] Pad002
  BaseFeature = -> Pad001
  Direction = (1,1,1)
  Length = 9
  Length2 = 100
  Placement = pos=(0,0,0) rot=(1,0,0;1.5708rad)
  Profile = -> Sketch003
  Type = 0
FEATURE [Sketcher::SketchObject] Sketch004
  ExternalGeometry = -> [Pad002]
  MapMode = 5
  Placement = pos=(0,49.3837,0) rot=(-1,0,0;1.5708rad)
  Support = -> [Pad002]
  sketch-geometry (4):
    g0: LineSegment StartX=37.5 StartY=-32.5321 StartZ=0 EndX=36 EndY=-32.5321 EndZ=0
    g1: LineSegment StartX=36 StartY=-32.5321 StartZ=0 EndX=36 EndY=-21.5321 EndZ=0
    g2: LineSegment StartX=36 StartY=-21.5321 StartZ=0 EndX=37.5 EndY=-21.5321 EndZ=0
    g3: LineSegment StartX=37.5 StartY=-21.5321 StartZ=0 EndX=37.5 EndY=-32.5321 EndZ=0
  constraints (11):
    c: Coincident(g0,g1)
    c: Coincident(g1,g2)
    c: Coincident(g2,g3)
    c: Coincident(g3,g0)
    c: Horizontal(g0)
    c: Horizontal(g2)
    c: Vertical(g1)
    c: Vertical(g3)
    c: Coincident(g0,g-3)
    c: DistanceX(g0,g0) = 1.5
    c: DistanceY(g1,g1) = 11
FEATURE [PartDesign::Pocket] Pocket001
  BaseFeature = -> Pad002
  Length = 5
  Length2 = 100
  Placement = pos=(0,0,0) rot=(1,0,0;1.5708rad)
  Profile = -> Sketch004
  Type = 0
FEATURE [Sketcher::SketchObject] Sketch005
  ExternalGeometry = -> [Pocket001]
  MapMode = 5
  Placement = pos=(0,49.3837,0) rot=(-1,0,0;1.5708rad)
  Support = -> [Pocket001]
  sketch-geometry (2):
    g0: Circle CenterX=7.5 CenterY=-20.5321 CenterZ=0 NormalX=0 NormalY=0 NormalZ=1 AngleXU=0 Radius=1.25
    g1: Circle CenterX=-32.5 CenterY=-21 CenterZ=0 NormalX=0 NormalY=0 NormalZ=1 AngleXU=0 Radius=1.5
  constraints (6):
    c: DistanceY(g-3,g0) = 12
    c: DistanceX(g0,g-4) = 30
    c: DistanceX(g1,g-4) = 70
    c: Radius(g0) = 1.25
    c: Radius(g1) = 1.5
    c: DistanceY(g1,g-1) = 21
FEATURE [PartDesign::Pocket] Pocket002
  BaseFeature = -> Pocket001
  Length = 5
  Length2 = 100
  Placement = pos=(0,0,0) rot=(1,0,0;1.5708rad)
  Profile = -> Sketch005
  Type = 0
FEATURE [PartDesign::Line] HoleAxis_1
  AttacherType = Attacher::AttachEngineLine
  Length = 3.52267
  MapMode = 19
  Placement = pos=(7.5,49.3837,20.5321) rot=(-1,0,0;1.5708rad)
  ResizeMode = 1
  Support = -> [Pocket002]
FEATURE [PartDesign::Line] HoleAxis_2
  AttacherType = Attacher::AttachEngineLine
  Length = 4.2272
  MapMode = 19
  Placement = pos=(-32.5,49.3837,21) rot=(-1,0,0;1.5708rad)
  ResizeMode = 1
  Support = -> [Pocket002]
FEATURE [Sketcher::SketchObject] Sketch006
  ExternalGeometry = -> [Pocket002]
  MapMode = 5
  Placement = pos=(0,0,0) rot=(1,0,0;3.14159rad)
  Support = -> [Pocket002]
  sketch-geometry (14):
    g0: ArcOfCircle CenterX=-33.75 CenterY=-52.5 CenterZ=0 NormalX=0 NormalY=0 NormalZ=1 AngleXU=0 Radius=1.75 StartAngle=0 EndAngle=3.14159
    g1: LineSegment StartX=-32 StartY=-52.5 StartZ=0 EndX=-32 EndY=-55 EndZ=0
    g2: LineSegment StartX=-32 StartY=-55 StartZ=0 EndX=-35.5 EndY=-55 EndZ=0
    g3: LineSegment StartX=-35.5 StartY=-55 StartZ=0 EndX=-35.5 EndY=-52.5 EndZ=0
    g4: LineSegment [constr] StartX=-13 StartY=23 StartZ=0 EndX=15 EndY=23 EndZ=0
    g5: LineSegment [constr] StartX=15 StartY=23 StartZ=0 EndX=15 EndY=-13 EndZ=0
    g6: LineSegment [constr] StartX=15 StartY=-13 StartZ=0 EndX=-13 EndY=-13 EndZ=0
    g7: LineSegment [constr] StartX=-13 StartY=-13 StartZ=0 EndX=-13 EndY=23 EndZ=0
    g8: Circle CenterX=-33 CenterY=50 CenterZ=0 NormalX=0 NormalY=0 NormalZ=1 AngleXU=0 Radius=1.5
    g9: Circle CenterX=-30.5 CenterY=-43 CenterZ=0 NormalX=0 NormalY=0 NormalZ=1 AngleXU=0 Radius=1.5
    g10: Circle CenterX=35 CenterY=51 CenterZ=0 NormalX=0 NormalY=0 NormalZ=1 AngleXU=0 Radius=1.75
    g11: Circle CenterX=-13 CenterY=23 CenterZ=0 NormalX=0 NormalY=0 NormalZ=1 AngleXU=0 Radius=1.5
    g12: Circle CenterX=-13 CenterY=-13 CenterZ=0 NormalX=0 NormalY=0 NormalZ=1 AngleXU=0 Radius=1.5
    g13: Circle CenterX=15 CenterY=-13 CenterZ=0 NormalX=0 NormalY=0 NormalZ=1 AngleXU=0 Radius=1.5
  constraints (38):
    c: Coincident(g1,g2)
    c: Coincident(g2,g3)
    c: Horizontal(g2)
    c: Vertical(g1)
    c: Vertical(g3)
    c: Tangent(g3,g0) = 1.5708
    c: Tangent(g1,g0) = 1.5708
    c: DistanceY(g3,g3) = 2.5
    c: DistanceX(g2,g2) = 3.5
    c: PointOnObject(g2,g-3)
    c: DistanceX(g-3,g2) = 2.5
    c: Coincident(g4,g5)
    c: Coincident(g5,g6)
    c: Coincident(g6,g7)
    c: Coincident(g7,g4)
    c: Horizontal(g4)
    c: Horizontal(g6)
    c: Vertical(g5)
    c: Vertical(g7)
    c: Coincident(g11,g4)
    c: Coincident(g12,g6)
    c: Coincident(g13,g5)
    c: Radius(g11) = 1.5
    c: Equal(g11,g12)
    c: Equal(g12,g13)
    c: Equal(g8,g11)
    c: Equal(g11,g9)
    c: DistanceY(g7,g7) = 36
    c: DistanceX(g6,g6) = 28
    c: DistanceX(g-3,g12) = 25
    c: DistanceY(g11,g-4) = 32
    c: DistanceY(g8,g-4) = 5
    c: DistanceX(g-4,g8) = 5
    c: DistanceY(g-3,g9) = 12
    c: DistanceX(g-3,g9) = 7.5
    c: DistanceX(g10,g-4) = 3
    c: Radius(g10) = 1.75
    c: DistanceY(g10,g-4) = 4
FEATURE [PartDesign::Pocket] Pocket003
  BaseFeature = -> Pocket002
  Length = 5
  Length2 = 100
  Placement = pos=(0,0,0) rot=(1,0,0;1.5708rad)
  Profile = -> Sketch006
  Type = 0
FEATURE [Sketcher::SketchObject] Sketch007
  ExternalGeometry = -> [Pocket003]
  MapMode = 5
  Placement = pos=(39.5,0,0) rot=(0.707107,0,0.707107;3.14159rad)
  Support = -> [Pocket003]
  sketch-geometry (31):
    g0: Circle CenterX=29 CenterY=50 CenterZ=0 NormalX=0 NormalY=0 NormalZ=1 AngleXU=0 Radius=1.75
    g1: Circle CenterX=20 CenterY=45 CenterZ=0 NormalX=0 NormalY=0 NormalZ=1 AngleXU=0 Radius=1.5
    g2: Circle CenterX=14.5 CenterY=-42.5 CenterZ=0 NormalX=0 NormalY=0 NormalZ=1 AngleXU=0 Radius=1.5
    g3: LineSegment StartX=7.5 StartY=45 StartZ=0 EndX=8.5 EndY=45 EndZ=0
    g4: LineSegment StartX=8.5 StartY=45 StartZ=0 EndX=8.5 EndY=38 EndZ=0
    g5: LineSegment StartX=8.5 StartY=38 StartZ=0 EndX=7.5 EndY=38 EndZ=0
    g6: LineSegment StartX=7.5 StartY=38 StartZ=0 EndX=7.5 EndY=45 EndZ=0
    g7: LineSegment StartX=4.5 StartY=45 StartZ=0 EndX=5.5 EndY=45 EndZ=0
    g8: LineSegment StartX=5.5 StartY=45 StartZ=0 EndX=5.5 EndY=38 EndZ=0
    g9: LineSegment StartX=5.5 StartY=38 StartZ=0 EndX=4.5 EndY=38 EndZ=0
    g10: LineSegment StartX=4.5 StartY=38 StartZ=0 EndX=4.5 EndY=45 EndZ=0
    g11: LineSegment StartX=7.5 StartY=-25 StartZ=0 EndX=8.5 EndY=-25 EndZ=0
    g12: LineSegment StartX=8.5 StartY=-25 StartZ=0 EndX=8.5 EndY=-32 EndZ=0
    g13: LineSegment StartX=8.5 StartY=-32 StartZ=0 EndX=7.5 EndY=-32 EndZ=0
    g14: LineSegment StartX=7.5 StartY=-32 StartZ=0 EndX=7.5 EndY=-25 EndZ=0
    g15: LineSegment StartX=4.5 StartY=-25 StartZ=0 EndX=5.5 EndY=-25 EndZ=0
    g16: LineSegment StartX=5.5 StartY=-25 StartZ=0 EndX=5.5 EndY=-32 EndZ=0
    g17: LineSegment StartX=5.5 StartY=-32 StartZ=0 EndX=4.5 EndY=-32 EndZ=0
    g18: LineSegment StartX=4.5 StartY=-32 StartZ=0 EndX=4.5 EndY=-25 EndZ=0
    g19: LineSegment [constr] StartX=5.5 StartY=38 StartZ=0 EndX=7.5 EndY=38 EndZ=0
    g20: LineSegment [constr] StartX=7.5 StartY=38 StartZ=0 EndX=7.5 EndY=-25 EndZ=0
    g21: LineSegment [constr] StartX=7.5 StartY=-25 StartZ=0 EndX=5.5 EndY=-25 EndZ=0
    g22: LineSegment [constr] StartX=5.5 StartY=-25 StartZ=0 EndX=5.5 EndY=38 EndZ=0
    g23: ArcOfCircle CenterX=27.25 CenterY=-52.5 CenterZ=0 NormalX=0 NormalY=0 NormalZ=1 AngleXU=0 Radius=1.75 StartAngle=2e-16 EndAngle=3.14159
    g24: LineSegment StartX=25.5 StartY=-52.5 StartZ=0 EndX=25.5 EndY=-55 EndZ=0
    g25: LineSegment StartX=25.5 StartY=-55 StartZ=0 EndX=29 EndY=-55 EndZ=0
    g26: LineSegment StartX=29 StartY=-55 StartZ=0 EndX=29 EndY=-52.5 EndZ=0
    g27: ArcOfCircle CenterX=31 CenterY=-34 CenterZ=0 NormalX=0 NormalY=0 NormalZ=1 AngleXU=0 Radius=1.5 StartAngle=3.14159 EndAngle=6.28319
    g28: LineSegment StartX=29.5 StartY=-34 StartZ=0 EndX=29.5 EndY=-29.5 EndZ=0
    g29: LineSegment StartX=29.5 StartY=-29.5 StartZ=0 EndX=32.5 EndY=-29.5 EndZ=0
    g30: LineSegment StartX=32.5 StartY=-29.5 StartZ=0 EndX=32.5 EndY=-34 EndZ=0
  constraints (87):
    c: Coincident(g3,g4)
    c: Coincident(g4,g5)
    c: Coincident(g5,g6)
    c: Coincident(g6,g3)
    c: Horizontal(g3)
    c: Horizontal(g5)
    c: Vertical(g4)
    c: Vertical(g6)
    c: Coincident(g7,g8)
    c: Coincident(g8,g9)
    c: Coincident(g9,g10)
    c: Coincident(g10,g7)
    c: Horizontal(g7)
    c: Horizontal(g9)
    c: Vertical(g8)
    c: Vertical(g10)
    c: Coincident(g11,g12)
    c: Coincident(g12,g13)
    c: Coincident(g13,g14)
    c: Coincident(g14,g11)
    c: Horizontal(g11)
    c: Horizontal(g13)
    c: Vertical(g12)
    c: Vertical(g14)
    c: Coincident(g15,g16)
    c: Coincident(g16,g17)
    c: Coincident(g17,g18)
    c: Coincident(g18,g15)
    c: Horizontal(g15)
    c: Horizontal(g17)
    c: Vertical(g16)
    c: Vertical(g18)
    c: Coincident(g19,g20)
    c: Coincident(g20,g21)
    c: Coincident(g21,g22)
    c: Coincident(g22,g19)
    c: Horizontal(g19)
    c: Horizontal(g21)
    c: Vertical(g20)
    c: Vertical(g22)
    c: Coincident(g19,g8)
    c: Coincident(g20,g11)
    c: Coincident(g5,g19)
    c: Coincident(g15,g21)
    c: Equal(g15,g11)
    c: Equal(g11,g5)
    c: Equal(g5,g9)
    c: Equal(g10,g6)
    c: Equal(g6,g18)
    c: Equal(g18,g14)
    c: DistanceX(g7,g7) = 1
    c: DistanceY(g10,g10) = 7
    c: DistanceX(g19,g19) = 2
    c: DistanceY(g7,g-3) = 10
    c: Radius(g1) = 1.5
    c: Equal(g1,g2)
    c: Vertical(g24)
    c: Coincident(g24,g25)
    c: Horizontal(g25)
    c: Coincident(g25,g26)
    c: Vertical(g26)
    c: Tangent(g24,g23) = -1.5708
    c: Tangent(g26,g23) = -1.5708
    c: DistanceY(g26,g26) = 2.5
    c: DistanceX(g25,g25) = 3.5
    c: PointOnObject(g25,g-4)
    c: DistanceX(g25,g-4) = 7
    c: DistanceX(g-3,g7) = 3
    c: Radius(g0) = 1.75
    c: DistanceX(g0,g-3) = 7
    c: DistanceY(g0,g-3) = 5
    c: DistanceX(g1,g-3) = 16
    c: DistanceY(g1,g-3) = 10
    c: DistanceY(g-4,g2) = 12.5
    c: DistanceX(g2,g-4) = 21.5
    c: DistanceY(g22,g22) = 63
    c: Vertical(g28)
    c: Coincident(g28,g29)
    c: Horizontal(g29)
    c: Coincident(g29,g30)
    c: Vertical(g30)
    c: Tangent(g27,g28) = 1.5708
    c: Tangent(g30,g27) = 1.5708
    c: DistanceX(g29,g29) = 3
    c: DistanceY(g30,g30) = 4.5
    c: DistanceX(g27,g-4) = 5
    c: DistanceY(g-4,g27) = 21
FEATURE [PartDesign::Pocket] Pocket004
  BaseFeature = -> Pocket003
  Length = 5
  Length2 = 100
  Placement = pos=(0,0,0) rot=(1,0,0;1.5708rad)
  Profile = -> Sketch007
  Type = 0
FEATURE [PartDesign::CoordinateSystem] LCS_1
  AttacherType = Attacher::AttachEngine3D
FEATURE [PartDesign::Line] HoleAxis_3  label="Screw_1"
  AttacherType = Attacher::AttachEngineLine
  Length = 4.2272
  MapMode = 19
  Placement = pos=(-13,-23,0) rot=(-1,0,0;3.14159rad)
  ResizeMode = 1
  Support = -> [Pocket004]
FEATURE [PartDesign::Line] HoleAxis_4  label="Screw_2"
  AttacherType = Attacher::AttachEngineLine
  Length = 4.2272
  MapMode = 19
  Placement = pos=(-13,13,0) rot=(-1,0,0;3.14159rad)
  ResizeMode = 1
  Support = -> [Pocket004]
FEATURE [PartDesign::Line] HoleAxis_5  label="Screw_3"
  AttacherType = Attacher::AttachEngineLine
  Length = 4.2272
  MapMode = 19
  Placement = pos=(15,13,0) rot=(-1,0,0;3.14159rad)
  ResizeMode = 1
  Support = -> [Pocket004]
FEATURE [PartDesign::Line] HoleAxis_6  label="Screw_4"
  AttacherType = Attacher::AttachEngineLine
  Length = 4.2272
  MapMode = 19
  Placement = pos=(39.5,-45,20) rot=(0.707107,0,0.707107;3.14159rad)
  ResizeMode = 1
  Support = -> [Pocket004]
FEATURE [PartDesign::Line] HoleAxis_7  label="Screw_5"
  AttacherType = Attacher::AttachEngineLine
  Length = 4.2272
  MapMode = 19
  Placement = pos=(39.5,42.5,14.5) rot=(0.707107,0,0.707107;3.14159rad)
  ResizeMode = 1
  Support = -> [Pocket004]
FEATURE [PartDesign::Line] HoleAxis_8  label="Screw_6"
  AttacherType = Attacher::AttachEngineLine
  Length = 4.2272
  MapMode = 19
  Placement = pos=(-33,-50,0) rot=(-1,0,0;3.14159rad)
  ResizeMode = 1
  Support = -> [Pocket004]
FEATURE [PartDesign::Line] HoleAxis_9  label="Screw_7"
  AttacherType = Attacher::AttachEngineLine
  Length = 4.2272
  MapMode = 19
  Placement = pos=(-30.5,43,0) rot=(-1,0,0;3.14159rad)
  ResizeMode = 1
  Support = -> [Pocket004]
FEATURE [PartDesign::Line] HoleAxis_10  label="Fastnr_1_R"
  AttacherType = Attacher::AttachEngineLine
  Length = 4.93174
  MapMode = 19
  Placement = pos=(35,-51,0) rot=(-1,0,0;3.14159rad)
  ResizeMode = 1
  Support = -> [Pocket004]
FEATURE [PartDesign::Line] HoleAxis_11  label="Fastnr_2_R"
  AttacherType = Attacher::AttachEngineLine
  Length = 3.90743
  MapMode = 19
  Placement = pos=(-33.75,52.5,0) rot=(-1,0,0;3.14159rad)
  ResizeMode = 1
  Support = -> [Pocket004]
FEATURE [PartDesign::Line] HoleAxis_12  label="Fastnr_3_R"
  AttacherType = Attacher::AttachEngineLine
  Length = 3.90743
  MapMode = 19
  Placement = pos=(39.5,52.5,27.25) rot=(0.707107,0,0.707107;3.14159rad)
  ResizeMode = 1
  Support = -> [Pocket004]
FEATURE [PartDesign::Line] HoleAxis_13  label="Fastnr_1_F"
  AttacherType = Attacher::AttachEngineLine
  Length = 4.93174
  MapMode = 19
  Placement = pos=(35,-51,1) rot=(-1,0,0;3.14159rad)
  ResizeMode = 1
  Support = -> [Pocket004]
FEATURE [PartDesign::Line] HoleAxis_14  label="Fastnr_2_F"
  AttacherType = Attacher::AttachEngineLine
  Length = 3.90743
  MapMode = 19
  Placement = pos=(-33.75,52.5,1) rot=(-1,0,0;3.14159rad)
  ResizeMode = 1
  Support = -> [Pocket004]
FEATURE [PartDesign::Line] HoleAxis_15  label="Fastnr_3_F"
  AttacherType = Attacher::AttachEngineLine
  Length = 3.90743
  MapMode = 19
  Placement = pos=(38.5,52.5,27.25) rot=(-0.707107,0,-0.707107;3.14159rad)
  ResizeMode = 1
  Support = -> [Pocket004]
FEATURE [Sketcher::SketchObject] Sketch008
  ExternalGeometry = -> [Pocket004]
  MapMode = 5
  Placement = pos=(0,0,1) rot=(0,0,1;3.14159rad)
  Support = -> [Pocket004]
  sketch-geometry (4):
    g0: Circle CenterX=33 CenterY=50 CenterZ=0 NormalX=0 NormalY=0 NormalZ=1 AngleXU=0 Radius=2.5
    g1: Circle CenterX=33 CenterY=50 CenterZ=0 NormalX=0 NormalY=0 NormalZ=1 AngleXU=0 Radius=1.5
    g2: Circle CenterX=30.5 CenterY=-43 CenterZ=0 NormalX=0 NormalY=0 NormalZ=1 AngleXU=0 Radius=2.5
    g3: Circle CenterX=30.5 CenterY=-43 CenterZ=0 NormalX=0 NormalY=0 NormalZ=1 AngleXU=0 Radius=1.5
  constraints (8):
    c: Coincident(g0,g-3)
    c: Coincident(g1,g0)
    c: Coincident(g2,g-4)
    c: Coincident(g3,g2)
    c: Radius(g0) = 2.5
    c: Equal(g0,g2)
    c: Equal(g1,g-3)
    c: Equal(g3,g-4)
FEATURE [PartDesign::Pad] Pad003
  BaseFeature = -> Pocket004
  Direction = (1,1,1)
  Length = 5
  Length2 = 100
  Placement = pos=(0,0,0) rot=(1,0,0;1.5708rad)
  Profile = -> Sketch008
  Type = 0
FEATURE [PartDesign::Line] HoleAxis_16
  AttacherType = Attacher::AttachEngineLine
  Length = 4.2272
  MapMode = 19
  Placement = pos=(-33,-50,6) rot=(0,0,1;3.14159rad)
  ResizeMode = 1
  Support = -> [Pad003]
FEATURE [PartDesign::Line] HoleAxis_17
  AttacherType = Attacher::AttachEngineLine
  Length = 4.2272
  MapMode = 19
  Placement = pos=(-30.5,43,6) rot=(0,0,1;3.14159rad)
  ResizeMode = 1
  Support = -> [Pad003]
FEATURE [PartDesign::Point] Label_1
  AttacherType = Attacher::AttachEnginePoint
  AttachmentOffset = pos=(0,-35,-3) rot=(0,0,1;0rad)
  MapMode = 39
  Placement = pos=(39.5,20,33) rot=(0,0,1;0rad)
  Support = -> [Pad003]
FEATURE [PartDesign::Body] Body
  Group = -> [Sketch,Pad,Sketch001,Pocket,DatumPlane,Sketch002,Pad001,Sketch003,Pad002,Sketch004,Pocket001,Sketch005,Pocket002,HoleAxis_1,HoleAxis_2,Sketch006,Pocket003,Sketch007,Pocket004,LCS_1,HoleAxis_3,HoleAxis_4,HoleAxis_5,HoleAxis_6,HoleAxis_7,HoleAxis_8,HoleAxis_9,HoleAxis_10,HoleAxis_11,HoleAxis_12,HoleAxis_13,HoleAxis_14,HoleAxis_15,Sketch008,Pad003,HoleAxis_16,HoleAxis_17,Label_1]
  Origin = -> Origin
  Tip = -> Pad003
---- part parts/top_shell.FCStd = doc fcstd_f1ec42ab7a32 ----
FCSTD DOCUMENT  (FreeCAD 0.19R23058 (Git))
Label: top_shell
License: All rights reserved
LicenseURL: http://en.wikipedia.org/wiki/All_rights_reserved
objects: Sketcher::SketchObject×6, PartDesign::Pad×4, PartDesign::Line×4, PartDesign::Pocket×2, PartDesign::Point×2, PartDesign::Body×1
note: 25 computed .brp shape members not serialized (recipe doc carries the construction recipe); baked Part::Feature solids carry a one-line shape summary decoded from their .brp

FEATURE [Sketcher::SketchObject] Sketch
  MapMode = 5
  Placement = pos=(0,0,0) rot=(1,0,0;1.5708rad)
  Support = -> [XZ_Plane]
  sketch-geometry (16):
    g0: LineSegment StartX=-35.75 StartY=-35 StartZ=0 EndX=-37.75 EndY=-35 EndZ=0
    g1: LineSegment StartX=-38.25 StartY=-34.5 StartZ=0 EndX=-38.25 EndY=-0.5 EndZ=0
    g2: LineSegment StartX=-37.75 StartY=0 StartZ=0 EndX=37.75 EndY=0 EndZ=0
    g3: LineSegment StartX=38.25 StartY=-0.5 StartZ=0 EndX=38.25 EndY=-6.5 EndZ=0
    g4: LineSegment StartX=38.25 StartY=-6.5 StartZ=0 EndX=38.05 EndY=-6.5 EndZ=0
    g5: LineSegment StartX=38.05 StartY=-6.5 StartZ=0 EndX=38.05 EndY=-0.5 EndZ=0
    g6: LineSegment StartX=37.75 StartY=-0.2 StartZ=0 EndX=-37.75 EndY=-0.2 EndZ=0
    g7: LineSegment StartX=-38.05 StartY=-0.5 StartZ=0 EndX=-38.05 EndY=-34.5 EndZ=0
    g8: LineSegment StartX=-37.75 StartY=-34.8 StartZ=0 EndX=-35.75 EndY=-34.8 EndZ=0
    g9: LineSegment StartX=-35.75 StartY=-34.8 StartZ=0 EndX=-35.75 EndY=-35 EndZ=0
    g10: ArcOfCircle CenterX=-37.75 CenterY=-34.5 CenterZ=0 NormalX=0 NormalY=0 NormalZ=1 AngleXU=0 Radius=0.5 StartAngle=3.14159 EndAngle=4.71239
    g11: ArcOfCircle CenterX=-37.75 CenterY=-34.5 CenterZ=0 NormalX=0 NormalY=0 NormalZ=1 AngleXU=0 Radius=0.3 StartAngle=3.14159 EndAngle=4.71239
    g12: ArcOfCircle CenterX=-37.75 CenterY=-0.5 CenterZ=0 NormalX=0 NormalY=0 NormalZ=1 AngleXU=0 Radius=0.3 StartAngle=1.5708 EndAngle=3.14159
    g13: ArcOfCircle CenterX=-37.75 CenterY=-0.5 CenterZ=0 NormalX=0 NormalY=0 NormalZ=1 AngleXU=0 Radius=0.5 StartAngle=1.5708 EndAngle=3.14159
    g14: ArcOfCircle CenterX=37.75 CenterY=-0.5 CenterZ=0 NormalX=0 NormalY=0 NormalZ=1 AngleXU=0 Radius=0.3 StartAngle=0 EndAngle=1.5708
    g15: ArcOfCircle CenterX=37.75 CenterY=-0.5 CenterZ=0 NormalX=0 NormalY=0 NormalZ=1 AngleXU=0 Radius=0.5 StartAngle=0 EndAngle=1.5708
  constraints (38):
    c: Horizontal(g0)
    c: Vertical(g1)
    c: Vertical(g3)
    c: Coincident(g3,g4)
    c: Horizontal(g4)
    c: Coincident(g4,g5)
    c: Vertical(g5)
    c: Vertical(g7)
    c: Horizontal(g8)
    c: Coincident(g8,g9)
    c: Coincident(g9,g0)
    c: Vertical(g9)
    c: Tangent(g0,g10) = 1.5708
    c: Tangent(g1,g10) = 1.5708
    c: Tangent(g8,g11) = -1.5708
    c: Tangent(g7,g11) = -1.5708
    c: Tangent(g7,g12) = -1.5708
    c: Tangent(g6,g12) = -1.5708
    c: Tangent(g1,g13) = 1.5708
    c: Tangent(g2,g13) = 1.5708
    c: Tangent(g5,g14) = -1.5708
    c: Tangent(g6,g14) = -1.5708
    c: Tangent(g3,g15) = 1.5708
    c: Tangent(g2,g15) = 1.5708
    c: DistanceY(g9,g9) = 0.2
    c: Coincident(g10,g11)
    c: Coincident(g13,g12)
    c: Coincident(g15,g14)
    c: Radius(g10) = 0.5
    c: DistanceX(g2,g2) = 75.5
    c: DistanceY(g1,g1) = 34
    c: PointOnObject(g2,g-1)
    c: Symmetric(g2,g2,g-2)
    c: Equal(g13,g15)
    c: Equal(g15,g10)
    c: Equal(g9,g4)
    c: DistanceY(g3,g3) = 6
    c: DistanceX(g0,g0) = 2
FEATURE [PartDesign::Pad] Pad
  Direction = (1,1,1)
  Length = 85
  Length2 = 100
  Midplane = true
  Placement = pos=(0,0,0) rot=(1,0,0;1.5708rad)
  Profile = -> Sketch
  Type = 0
FEATURE [Sketcher::SketchObject] Sketch001
  AttachmentOffset = pos=(0,0,-1) rot=(0,0,1;0rad)
  ExternalGeometry = -> [Pad]
  MapMode = 5
  Placement = pos=(0,0,-1) rot=(0,0,1;3.14159rad)
  Support = -> [Pad]
  sketch-geometry (14):
    g0: ArcOfCircle CenterX=37.75 CenterY=42.5 CenterZ=0 NormalX=0 NormalY=0 NormalZ=1 AngleXU=0 Radius=0.5 StartAngle=0 EndAngle=1.5708
    g1: ArcOfCircle CenterX=37.75 CenterY=42.5 CenterZ=0 NormalX=0 NormalY=0 NormalZ=1 AngleXU=0 Radius=0.3 StartAngle=0 EndAngle=1.5708
    g2: LineSegment StartX=38.05 StartY=42.5 StartZ=0 EndX=38.25 EndY=42.5 EndZ=0
    g3: LineSegment StartX=37.75 StartY=43 StartZ=0 EndX=28.75 EndY=43 EndZ=0
    g4: LineSegment StartX=28.75 StartY=43 StartZ=0 EndX=28.75 EndY=42.8 EndZ=0
    g5: LineSegment StartX=28.75 StartY=42.8 StartZ=0 EndX=37.75 EndY=42.8 EndZ=0
    g6: LineSegment [constr] StartX=38.05 StartY=42.5 StartZ=0 EndX=37.75 EndY=42.5 EndZ=0
    g7: ArcOfCircle CenterX=37.75 CenterY=-42.5 CenterZ=0 NormalX=0 NormalY=0 NormalZ=1 AngleXU=0 Radius=0.5 StartAngle=4.71239 EndAngle=6.28319
    g8: ArcOfCircle CenterX=37.75 CenterY=-42.5 CenterZ=0 NormalX=0 NormalY=0 NormalZ=1 AngleXU=0 Radius=0.3 StartAngle=4.71239 EndAngle=6.28319
    g9: LineSegment StartX=38.05 StartY=-42.5 StartZ=0 EndX=38.25 EndY=-42.5 EndZ=0
    g10: LineSegment StartX=37.75 StartY=-42.8 StartZ=0 EndX=28.75 EndY=-42.8 EndZ=0
    g11: LineSegment StartX=28.75 StartY=-42.8 StartZ=0 EndX=28.75 EndY=-43 EndZ=0
    g12: LineSegment StartX=28.75 StartY=-43 StartZ=0 EndX=37.75 EndY=-43 EndZ=0
    g13: LineSegment [constr] StartX=37.75 StartY=-42.5 StartZ=0 EndX=38.05 EndY=-42.5 EndZ=0
  constraints (36):
    c: Coincident(g1,g0)
    c: Horizontal(g2)
    c: Horizontal(g3)
    c: Coincident(g3,g4)
    c: Vertical(g4)
    c: Coincident(g4,g5)
    c: Horizontal(g5)
    c: Tangent(g3,g0) = -1.5708
    c: Tangent(g5,g1) = 1.5708
    c: Coincident(g2,g1)
    c: Coincident(g2,g0)
    c: Coincident(g6,g1)
    c: Horizontal(g6)
    c: Coincident(g0,g6)
    c: Coincident(g0,g-3)
    c: Radius(g0) = 0.5
    c: DistanceX(g2,g2) = 0.2
    c: DistanceX(g3,g3) = 9
    c: Coincident(g8,g7)
    c: Horizontal(g10)
    c: Coincident(g10,g11)
    c: Vertical(g11)
    c: Coincident(g11,g12)
    c: Horizontal(g12)
    c: Tangent(g10,g8) = 1.5708
    c: Tangent(g12,g7) = -1.5708
    c: Coincident(g8,g9)
    c: Equal(g2,g9)
    c: Equal(g7,g0)
    c: Coincident(g9,g7)
    c: Horizontal(g9)
    c: Coincident(g7,g-4)
    c: DistanceX(g12,g12) = 9
    c: Coincident(g13,g7)
    c: Coincident(g13,g8)
    c: Horizontal(g13)
FEATURE [PartDesign::Pad] Pad001
  BaseFeature = -> Pad
  Direction = (1,1,1)
  Length = 26
  Length2 = 100
  Placement = pos=(0,0,0) rot=(1,0,0;1.5708rad)
  Profile = -> Sketch001
  Reversed = true
  Type = 0
FEATURE [Sketcher::SketchObject] Sketch002
  AttachmentOffset = pos=(0,0,-1) rot=(0,0,1;0rad)
  ExternalGeometry = -> [Pad001]
  MapMode = 5
  Placement = pos=(-37.25,0,2e-16) rot=(0.707107,0,-0.707107;3.14159rad)
  Support = -> [Pad001]
  sketch-geometry (16):
    g0: ArcOfCircle CenterX=0.5 CenterY=42.7 CenterZ=0 NormalX=0 NormalY=0 NormalZ=1 AngleXU=0 Radius=0.5 StartAngle=1.5708 EndAngle=3.14159
    g1: ArcOfCircle CenterX=0.5 CenterY=42.7 CenterZ=0 NormalX=0 NormalY=0 NormalZ=1 AngleXU=0 Radius=0.3 StartAngle=1.5708 EndAngle=3.14159
    g2: LineSegment StartX=-5.88e-14 StartY=42.7 StartZ=0 EndX=-5.88e-14 EndY=42.5 EndZ=0
    g3: LineSegment StartX=-5.88e-14 StartY=42.5 StartZ=0 EndX=0.2 EndY=42.5 EndZ=0
    g4: LineSegment StartX=0.2 StartY=42.5 StartZ=0 EndX=0.2 EndY=42.7 EndZ=0
    g5: LineSegment StartX=0.5 StartY=43 StartZ=0 EndX=10.5 EndY=43 EndZ=0
    g6: LineSegment StartX=10.5 StartY=43 StartZ=0 EndX=10.5 EndY=43.2 EndZ=0
    g7: LineSegment StartX=10.5 StartY=43.2 StartZ=0 EndX=0.5 EndY=43.2 EndZ=0
    g8: ArcOfCircle CenterX=0.5 CenterY=-42.7 CenterZ=0 NormalX=0 NormalY=0 NormalZ=1 AngleXU=0 Radius=0.5 StartAngle=3.14159 EndAngle=4.71239
    g9: ArcOfCircle CenterX=0.5 CenterY=-42.7 CenterZ=0 NormalX=0 NormalY=0 NormalZ=1 AngleXU=0 Radius=0.3 StartAngle=3.14159 EndAngle=4.71239
    g10: LineSegment StartX=3.367e-13 StartY=-42.7 StartZ=0 EndX=3.367e-13 EndY=-42.5 EndZ=0
    g11: LineSegment StartX=3.367e-13 StartY=-42.5 StartZ=0 EndX=0.2 EndY=-42.5 EndZ=0
    g12: LineSegment StartX=0.2 StartY=-42.5 StartZ=0 EndX=0.2 EndY=-42.7 EndZ=0
    g13: LineSegment StartX=0.5 StartY=-43 StartZ=0 EndX=4.5 EndY=-43 EndZ=0
    g14: LineSegment StartX=4.5 StartY=-43 StartZ=0 EndX=4.5 EndY=-43.2 EndZ=0
    g15: LineSegment StartX=4.5 StartY=-43.2 StartZ=0 EndX=0.5 EndY=-43.2 EndZ=0
  constraints (40):
    c: Coincident(g1,g0)
    c: Vertical(g2)
    c: Coincident(g2,g3)
    c: Horizontal(g3)
    c: Coincident(g3,g4)
    c: Vertical(g4)
    c: Horizontal(g5)
    c: Coincident(g5,g6)
    c: Vertical(g6)
    c: Coincident(g6,g7)
    c: Horizontal(g7)
    c: Tangent(g2,g0) = -1.5708
    c: Tangent(g4,g1) = 1.5708
    c: Tangent(g1,g5) = 1.5708
    c: Tangent(g7,g0) = -1.5708
    c: DistanceY(g6,g6) = 0.2
    c: Radius(g0) = 0.5
    c: Coincident(g2,g-3)
    c: DistanceY(g2,g2) = 0.2
    c: Coincident(g9,g8)
    c: Vertical(g10)
    c: Coincident(g10,g11)
    c: Horizontal(g11)
    c: Coincident(g11,g12)
    c: Vertical(g12)
    c: Horizontal(g13)
    c: Coincident(g13,g14)
    c: Vertical(g14)
    c: Coincident(g14,g15)
    c: Horizontal(g15)
    c: Tangent(g8,g10) = 1.5708
    c: Tangent(g12,g9) = -1.5708
    c: Tangent(g9,g13) = -1.5708
    c: Tangent(g8,g15) = 1.5708
    c: Equal(g8,g0)
    c: Equal(g11,g3)
    c: Equal(g10,g2)
    c: DistanceX(g7,g7) = 10
    c: Coincident(g10,g-4)
    c: DistanceX(g15,g15) = 4
FEATURE [PartDesign::Pad] Pad002
  BaseFeature = -> Pad001
  Direction = (1,1,1)
  Length = 73
  Length2 = 100
  Placement = pos=(0,0,0) rot=(1,0,0;1.5708rad)
  Profile = -> Sketch002
  Reversed = true
  Type = 0
FEATURE [Sketcher::SketchObject] Sketch003
  ExternalGeometry = -> [Pad002]
  MapMode = 5
  Placement = pos=(-28.75,0,0) rot=(0.707107,0,0.707107;3.14159rad)
  Support = -> [Pad002]
  sketch-geometry (7):
    g0: ArcOfCircle CenterX=-27 CenterY=44.3 CenterZ=0 NormalX=0 NormalY=0 NormalZ=1 AngleXU=0 Radius=1.3 StartAngle=3.14159 EndAngle=4.71239
    g1: ArcOfCircle CenterX=-27 CenterY=44.3 CenterZ=0 NormalX=0 NormalY=0 NormalZ=1 AngleXU=0 Radius=1.5 StartAngle=3.14159 EndAngle=4.71239
    g2: LineSegment StartX=-28.3 StartY=44.3 StartZ=0 EndX=-28.3 EndY=61.3 EndZ=0
    g3: LineSegment StartX=-28.3 StartY=61.3 StartZ=0 EndX=-28.5 EndY=61.3 EndZ=0
    g4: LineSegment StartX=-28.5 StartY=61.3 StartZ=0 EndX=-28.5 EndY=44.3 EndZ=0
    g5: LineSegment StartX=-27 StartY=43 StartZ=0 EndX=-27 EndY=42.8 EndZ=0
    g6: LineSegment [constr] StartX=-27 StartY=43 StartZ=0 EndX=-27 EndY=44.3 EndZ=0
  constraints (18):
    c: Coincident(g1,g0)
    c: Vertical(g2)
    c: Coincident(g2,g3)
    c: Horizontal(g3)
    c: Coincident(g3,g4)
    c: Vertical(g4)
    c: Tangent(g2,g0) = 1.5708
    c: Tangent(g4,g1) = -1.5708
    c: Vertical(g5)
    c: Coincident(g0,g5)
    c: Coincident(g5,g1)
    c: DistanceY(g5,g5) = 0.2
    c: Coincident(g6,g0)
    c: Coincident(g6,g0)
    c: Vertical(g6)
    c: Coincident(g1,g-3)
    c: Radius(g1) = 1.5
    c: DistanceY(g4,g4) = 17
FEATURE [PartDesign::Pad] Pad003
  BaseFeature = -> Pad002
  Direction = (1,1,1)
  Length = 8.5
  Length2 = 100
  Placement = pos=(0,0,0) rot=(1,0,0;1.5708rad)
  Profile = -> Sketch003
  Reversed = true
  Type = 0
FEATURE [Sketcher::SketchObject] Sketch004
  ExternalGeometry = -> [Pad003]
  MapMode = 5
  Placement = pos=(0,43,0) rot=(-1,0,0;1.5708rad)
  Support = -> [Pad003]
  sketch-geometry (1):
    g0: Circle CenterX=-32.75 CenterY=15 CenterZ=0 NormalX=0 NormalY=0 NormalZ=1 AngleXU=0 Radius=1.75
  constraints (3):
    c: DistanceY(g0,g-3) = 12
    c: DistanceX(g0,g-3) = 4
    c: Radius(g0) = 1.75
FEATURE [PartDesign::Pocket] Pocket
  BaseFeature = -> Pad003
  Length = 5
  Length2 = 100
  Placement = pos=(0,0,0) rot=(1,0,0;1.5708rad)
  Profile = -> Sketch004
  Type = 0
FEATURE [PartDesign::Line] HoleAxis_1
  AttacherType = Attacher::AttachEngineLine
  Length = 4.93174
  MapMode = 19
  Placement = pos=(-32.75,42.8,-15) rot=(-1,0,0;1.5708rad)
  ResizeMode = 1
  Support = -> [Pocket]
FEATURE [PartDesign::Line] HoleAxis_2
  AttacherType = Attacher::AttachEngineLine
  Length = 4.93174
  MapMode = 19
  Placement = pos=(-32.75,43,-15) rot=(-1,0,0;1.5708rad)
  ResizeMode = 1
  Support = -> [Pocket]
FEATURE [Sketcher::SketchObject] Sketch005
  ExternalGeometry = -> [Pocket]
  MapMode = 5
  Placement = pos=(-6.2e-15,0,-28.3) rot=(0,0,1;3.14159rad)
  Support = -> [Pocket]
  sketch-geometry (1):
    g0: Circle CenterX=33.25 CenterY=56.8 CenterZ=0 NormalX=0 NormalY=0 NormalZ=1 AngleXU=0 Radius=1.75
  constraints (3):
    c: Radius(g0) = 1.75
    c: DistanceY(g0,g-3) = 4.5
    c: DistanceX(g0,g-3) = 4
FEATURE [PartDesign::Pocket] Pocket001
  BaseFeature = -> Pocket
  Length = 5
  Length2 = 100
  Placement = pos=(0,0,0) rot=(1,0,0;1.5708rad)
  Profile = -> Sketch005
  Type = 0
FEATURE [PartDesign::Line] HoleAxis_3
  AttacherType = Attacher::AttachEngineLine
  Length = 4.93174
  MapMode = 19
  Placement = pos=(-33.25,-56.8,-28.3) rot=(0,0,1;3.14159rad)
  ResizeMode = 1
  Support = -> [Pocket001]
FEATURE [PartDesign::Line] HoleAxis_4
  AttacherType = Attacher::AttachEngineLine
  Length = 4.93174
  MapMode = 19
  Placement = pos=(-33.25,-56.8,-28.5) rot=(0,0,1;3.14159rad)
  ResizeMode = 1
  Support = -> [Pocket001]
FEATURE [PartDesign::Point] Label_1
  AttacherType = Attacher::AttachEnginePoint
  AttachmentOffset = pos=(5,0,0) rot=(0,0,1;0rad)
  MapMode = 39
  Placement = pos=(-32.25,-43.2,-10.5) rot=(0,0,1;0rad)
  Support = -> [Pocket001]
FEATURE [PartDesign::Point] Point_1  label="Label_2"
  AttacherType = Attacher::AttachEnginePoint
  AttachmentOffset = pos=(3,1,0) rot=(0,0,1;0rad)
  MapMode = 39
  Placement = pos=(-34.75,-41.5,0) rot=(0,0,1;0rad)
  Support = -> [Pocket001]
FEATURE [PartDesign::Body] Body
  Group = -> [Sketch,Pad,Sketch001,Pad001,Sketch002,Pad002,Sketch003,Pad003,Sketch004,Pocket,HoleAxis_1,HoleAxis_2,Sketch005,Pocket001,HoleAxis_3,HoleAxis_4,Label_1,Point_1]
  Origin = -> Origin
  Tip = -> Pocket001
